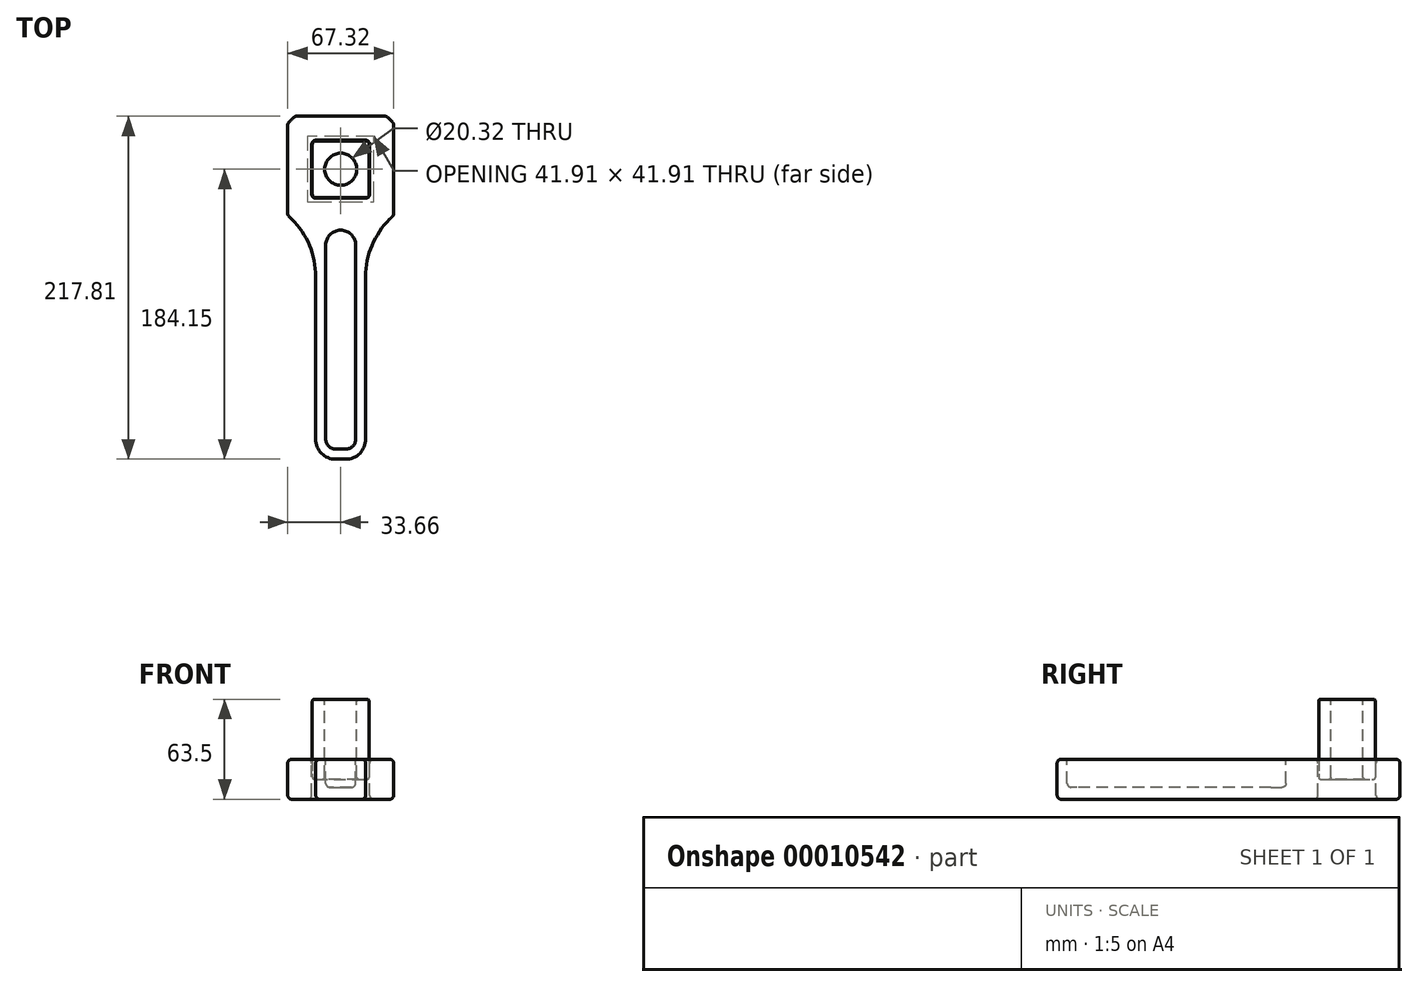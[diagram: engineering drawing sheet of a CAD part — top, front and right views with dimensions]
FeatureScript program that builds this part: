
annotation { "Feature Type Name" : "Feature", "Feature Type Description" : "" }
export const myFeature = defineFeature(function(context is Context, id is Id, definition is map)
    precondition{}
    {
        {
            var Q0;
            Q0=qCreatedBy(makeId("Top.planeOp"),FACE);
            var sketch = newSketch(context, id + "F0", { "sketchPlane" : qUnion([Q0])});
            skCircle(sketch, "E0", {"center": v(0, 0) * mm, "radius": 44.45 * mm});
            skLineSegment(sketch, "E1.bottom", {"start": v(-15.87, 0) * mm, "end": v(15.87, 0) * mm});
            skLineSegment(sketch, "E1.top", {"start": v(-15.87, -184.15) * mm, "end": v(15.88, -184.15) * mm});
            skLineSegment(sketch, "E1.left", {"start": v(-15.87, 0) * mm, "end": v(-15.87, -184.15) * mm});
            skLineSegment(sketch, "E1.right", {"start": v(15.88, 0) * mm, "end": v(15.88, -184.15) * mm});
            skLineSegment(sketch, "E2", {"start": v(0, 0) * mm, "end": v(0, -184.15) * mm, "construction": true});
            skSolve(sketch);
        }
        {
            var Q0;
            Q0 = qSketchRegion(id + "F0", true);
            extrude(context, id + "F1", {"entities" : qUnion([Q0]), "depth" : 25.4 * mm, "symmetric" : true});
        }
        {
            var Q0;
            Q0=makeQuery(id+"F1.opExtrude","CAP_FACE",FACE,{"disambiguationData":[OSD([sQuery(id+"F0.wireOp",EDGE,"E0"),sQuery(id+"F0.wireOp",EDGE,"E1.top"),sQuery(id+"F0.wireOp",EDGE,"E1.left"),sQuery(id+"F0.wireOp",EDGE,"E1.right")])],"isStart":false});
            var sketch = newSketch(context, id + "F2", { "sketchPlane" : qUnion([Q0])});
            skLineSegment(sketch, "E3.bottom", {"start": v(-18.42, 18.41) * mm, "end": v(18.41, 18.41) * mm});
            skLineSegment(sketch, "E3.top", {"start": v(-18.41, -18.41) * mm, "end": v(18.41, -18.41) * mm});
            skLineSegment(sketch, "E3.left", {"start": v(-18.41, 18.41) * mm, "end": v(-18.41, -18.41) * mm});
            skLineSegment(sketch, "E3.right", {"start": v(18.41, 18.41) * mm, "end": v(18.42, -18.41) * mm});
            skLineSegment(sketch, "E4", {"start": v(0, 0) * mm, "end": v(0, -18.41) * mm, "construction": true});
            skLineSegment(sketch, "E5", {"start": v(0, 0) * mm, "end": v(18.41, 0) * mm, "construction": true});
            skSolve(sketch);
        }
        {
            var Q0;
            Q0 = qSketchRegion(id + "F2", true);
            extrude(context, id + "F3", {"entities" : qUnion([Q0]), "operationType" : NewBodyOperationType.REMOVE, "endBound" : BoundingType.UP_TO_NEXT, "oppositeDirection" : true, "depth" : 25.4 * mm});
        }
        {
            var Q0;
            Q0=makeQuery(id+"F1.opExtrude","SWEPT_EDGE",EDGE,{"disambiguationData":[OSD([sQuery(id+"F0.wireOp",EDGE,"E0"),sQuery(id+"F0.wireOp",EDGE,"E1.right")])]});
            var Q1;
            Q1=makeQuery(id+"F1.opExtrude","SWEPT_EDGE",EDGE,{"disambiguationData":[OSD([sQuery(id+"F0.wireOp",EDGE,"E0"),sQuery(id+"F0.wireOp",EDGE,"E1.left")])]});
            fillet(context, id + "F4", {"entities" : qUnion([Q0, Q1]), "radius" : 50.8 * mm, "tangentPropagation" : true, "allowEdgeOverflow" : false});
        }
        {
            var Q0;
            Q0=makeQuery(id+"F1.opExtrude","SWEPT_EDGE",EDGE,{"disambiguationData":[OSD([sQuery(id+"F0.wireOp",EDGE,"E1.top"),sQuery(id+"F0.wireOp",EDGE,"E1.right")])]});
            var Q1;
            Q1=makeQuery(id+"F1.opExtrude","SWEPT_EDGE",EDGE,{"disambiguationData":[OSD([sQuery(id+"F0.wireOp",EDGE,"E1.top"),sQuery(id+"F0.wireOp",EDGE,"E1.left")])]});
            fillet(context, id + "F5", {"entities" : qUnion([Q0, Q1]), "radius" : 12.7 * mm, "tangentPropagation" : true, "allowEdgeOverflow" : false});
        }
        {
            var Q0;
            Q0=makeQuery(id+"F1.opExtrude","CAP_FACE",FACE,{"disambiguationData":[OSD([sQuery(id+"F0.wireOp",EDGE,"E0"),sQuery(id+"F0.wireOp",EDGE,"E1.top"),sQuery(id+"F0.wireOp",EDGE,"E1.left"),sQuery(id+"F0.wireOp",EDGE,"E1.right")])],"isStart":false});
            var sketch = newSketch(context, id + "F6", { "sketchPlane" : qUnion([Q0])});
            skLineSegment(sketch, "E6.1", {"start": v(9.53, -48.26) * mm, "end": v(9.53, -171.45) * mm});
            skArc(sketch, "E6.2", {"start": v(3.18, -177.8) * mm, "mid": v(7.67, -175.94) * mm, "end": v(9.53, -171.45) * mm});
            skLineSegment(sketch, "E6.4", {"start": v(-9.53, -48.26) * mm, "end": v(-9.53, -171.45) * mm});
            skArc(sketch, "E6.5", {"start": v(-9.53, -171.45) * mm, "mid": v(-7.67, -175.94) * mm, "end": v(-3.17, -177.8) * mm});
            skLineSegment(sketch, "E6.6", {"start": v(-3.17, -177.8) * mm, "end": v(3.18, -177.8) * mm});
            skArc(sketch, "E7", {"start": v(-9.53, -48.26) * mm, "mid": v(0, -38.74) * mm, "end": v(9.53, -48.26) * mm});
            skSolve(sketch);
        }
        {
            var Q0;
            Q0 = qSketchRegion(id + "F6", true);
            extrude(context, id + "F7", {"entities" : qUnion([Q0]), "operationType" : NewBodyOperationType.REMOVE, "oppositeDirection" : true, "depth" : 17.78 * mm});
        }
        {
            var Q0;
            Q0=makeQuery(id+"F1.opExtrude","CAP_FACE",FACE,{"disambiguationData":[OSD([sQuery(id+"F0.wireOp",EDGE,"E0"),sQuery(id+"F0.wireOp",EDGE,"E1.top"),sQuery(id+"F0.wireOp",EDGE,"E1.left"),sQuery(id+"F0.wireOp",EDGE,"E1.right")])],"isStart":false});
            var sketch = newSketch(context, id + "F8", { "sketchPlane" : qUnion([Q0])});
            skLineSegment(sketch, "E8.0", {"start": v(33.65, 33.66) * mm, "end": v(33.66, -29.04) * mm});
            skLineSegment(sketch, "E8.1", {"start": v(-33.66, 33.66) * mm, "end": v(33.65, 33.66) * mm});
            skLineSegment(sketch, "E8.2", {"start": v(-33.66, 33.66) * mm, "end": v(-33.66, -29.04) * mm});
            skSolve(sketch);
        }
        {
            var Q0;
            {var subQ0=sQuery(id+"F8.wireOp",EDGE,"E8.2");var subQ1=makeQuery(id+"F1.opExtrude","CAP_EDGE",EDGE,{"disambiguationData":[OSD([sQuery(id+"F0.wireOp",EDGE,"E0")])],"isStart":false});var subQ2=makeQuery(id+"F8.imprint","INTERSECT",VERTEX,{"disambiguationData":[OD(0.0)],"derivedFrom":[subQ1,subQ0]});Q0=makeQuery(id+"F8.imprint","IMPRINT",FACE,{"disambiguationData":[TD([[makeQuery(id+"F8.imprint","IMPRINT",EDGE,{"disambiguationData":[TD([[subQ2,1.0]])],"derivedFrom":subQ0}),-1.0]])]});}
            var Q1;
            {var subQ0=sQuery(id+"F8.wireOp",EDGE,"E8.1");var subQ1=makeQuery(id+"F1.opExtrude","CAP_EDGE",EDGE,{"disambiguationData":[OSD([sQuery(id+"F0.wireOp",EDGE,"E0")])],"isStart":false});var subQ2=makeQuery(id+"F8.imprint","INTERSECT",VERTEX,{"disambiguationData":[OD(0.0)],"derivedFrom":[subQ1,subQ0]});Q1=makeQuery(id+"F8.imprint","IMPRINT",FACE,{"disambiguationData":[TD([[makeQuery(id+"F8.imprint","IMPRINT",EDGE,{"disambiguationData":[TD([[subQ2,-1.0]])],"derivedFrom":subQ0}),1.0]])]});}
            var Q2;
            {var subQ0=sQuery(id+"F8.wireOp",EDGE,"E8.0");var subQ1=makeQuery(id+"F1.opExtrude","CAP_EDGE",EDGE,{"disambiguationData":[OSD([sQuery(id+"F0.wireOp",EDGE,"E0")])],"isStart":false});var subQ2=makeQuery(id+"F8.imprint","INTERSECT",VERTEX,{"disambiguationData":[OD(0.0)],"derivedFrom":[subQ1,subQ0]});Q2=makeQuery(id+"F8.imprint","IMPRINT",FACE,{"disambiguationData":[TD([[makeQuery(id+"F8.imprint","IMPRINT",EDGE,{"disambiguationData":[TD([[subQ2,1.0]])],"derivedFrom":subQ0}),1.0]])]});}
            extrude(context, id + "F9", {"entities" : qUnion([Q0, Q1, Q2]), "operationType" : NewBodyOperationType.REMOVE, "endBound" : BoundingType.UP_TO_NEXT, "oppositeDirection" : true, "depth" : 25.4 * mm});
        }
        {
            var Q0;
            Q0=makeQuery(id+"F3.boolean.opBoolean","COPY",FACE,{"derivedFrom":makeQuery(id+"F3.opExtrude","SWEPT_FACE",FACE,{"disambiguationData":[OSD([sQuery(id+"F2.wireOp",EDGE,"E3.bottom")])]})});
            var Q1;
            Q1=makeQuery(id+"F3.boolean.opBoolean","COPY",FACE,{"derivedFrom":makeQuery(id+"F3.opExtrude","SWEPT_FACE",FACE,{"disambiguationData":[OSD([sQuery(id+"F2.wireOp",EDGE,"E3.right")])]})});
            var Q2;
            Q2=makeQuery(id+"F3.boolean.opBoolean","COPY",FACE,{"derivedFrom":makeQuery(id+"F3.opExtrude","SWEPT_FACE",FACE,{"disambiguationData":[OSD([sQuery(id+"F2.wireOp",EDGE,"E3.left")])]})});
            var Q3;
            Q3=makeQuery(id+"F3.boolean.opBoolean","COPY",FACE,{"derivedFrom":makeQuery(id+"F3.opExtrude","SWEPT_FACE",FACE,{"disambiguationData":[OSD([sQuery(id+"F2.wireOp",EDGE,"E3.top")])]})});
            fillet(context, id + "F10", {"entities" : qUnion([Q0, Q1, Q2, Q3]), "radius" : 2.54 * mm, "tangentPropagation" : true, "allowEdgeOverflow" : false});
        }
        {
            var Q0;
            Q0=makeQuery(id+"F1.opExtrude","CAP_EDGE",EDGE,{"disambiguationData":[OSD([sQuery(id+"F0.wireOp",EDGE,"E1.left")])],"isStart":false});
            var Q1;
            Q1=makeQuery(id+"F7.boolean.opBoolean","COPY",FACE,{"derivedFrom":makeQuery(id+"F7.opExtrude","CAP_FACE",FACE,{"disambiguationData":[OSD([sQuery(id+"F6.wireOp",EDGE,"E6.1"),sQuery(id+"F6.wireOp",EDGE,"E6.2"),sQuery(id+"F6.wireOp",EDGE,"E6.4"),sQuery(id+"F6.wireOp",EDGE,"E6.5"),sQuery(id+"F6.wireOp",EDGE,"E6.6"),sQuery(id+"F6.wireOp",EDGE,"E7")])],"isStart":false})});
            var Q2;
            Q2=makeQuery(id+"F7.boolean.opBoolean","COPY",EDGE,{"derivedFrom":makeQuery(id+"F7.opExtrude","CAP_EDGE",EDGE,{"disambiguationData":[OSD([sQuery(id+"F6.wireOp",EDGE,"E7")])],"isStart":true})});
            var Q3;
            Q3=makeQuery(id+"F1.opExtrude","CAP_EDGE",EDGE,{"disambiguationData":[OSD([sQuery(id+"F0.wireOp",EDGE,"E1.left")])],"isStart":true});
            var Q4;
            Q4=makeQuery(id+"F9.boolean.opBoolean","COPY",FACE,{"derivedFrom":makeQuery(id+"F9.opExtrude","SWEPT_FACE",FACE,{"disambiguationData":[OSD([sQuery(id+"F8.wireOp",EDGE,"E8.2")])]})});
            var Q5;
            {var subQ0=sQuery(id+"F0.wireOp",EDGE,"E1.right");var subQ1=sQuery(id+"F0.wireOp",EDGE,"E1.left");var subQ2=sQuery(id+"F0.wireOp",EDGE,"E1.top");var subQ3=sQuery(id+"F0.wireOp",EDGE,"E0");Q5=makeQuery(id+"F9.boolean.opBoolean","SPLIT",FACE,{"disambiguationData":[TD([makeQuery(id+"F1.opExtrude","CAP_FACE",FACE,{"disambiguationData":[OSD([subQ3,subQ2,subQ1,subQ0])],"isStart":true}),makeQuery(id+"F1.opExtrude","CAP_FACE",FACE,{"disambiguationData":[OSD([subQ3,subQ2,subQ1,subQ0])],"isStart":false}),makeQuery(id+"F9.opExtrude","SWEPT_FACE",FACE,{"disambiguationData":[OSD([sQuery(id+"F8.wireOp",EDGE,"E8.1")])]}),makeQuery(id+"F9.opExtrude","SWEPT_FACE",FACE,{"disambiguationData":[OSD([sQuery(id+"F8.wireOp",EDGE,"E8.2")])]})])],"derivedFrom":makeQuery(id+"F1.opExtrude","SWEPT_FACE",FACE,{"disambiguationData":[OSD([subQ3])]})});}
            var Q6;
            Q6=makeQuery(id+"F9.boolean.opBoolean","COPY",FACE,{"derivedFrom":makeQuery(id+"F9.opExtrude","SWEPT_FACE",FACE,{"disambiguationData":[OSD([sQuery(id+"F8.wireOp",EDGE,"E8.1")])]})});
            var Q7;
            {var subQ0=sQuery(id+"F0.wireOp",EDGE,"E1.right");var subQ1=sQuery(id+"F0.wireOp",EDGE,"E1.left");var subQ2=sQuery(id+"F0.wireOp",EDGE,"E1.top");var subQ3=sQuery(id+"F0.wireOp",EDGE,"E0");Q7=makeQuery(id+"F9.boolean.opBoolean","SPLIT",FACE,{"disambiguationData":[TD([makeQuery(id+"F1.opExtrude","CAP_FACE",FACE,{"disambiguationData":[OSD([subQ3,subQ2,subQ1,subQ0])],"isStart":true}),makeQuery(id+"F1.opExtrude","CAP_FACE",FACE,{"disambiguationData":[OSD([subQ3,subQ2,subQ1,subQ0])],"isStart":false}),makeQuery(id+"F9.opExtrude","SWEPT_FACE",FACE,{"disambiguationData":[OSD([sQuery(id+"F8.wireOp",EDGE,"E8.0")])]}),makeQuery(id+"F9.opExtrude","SWEPT_FACE",FACE,{"disambiguationData":[OSD([sQuery(id+"F8.wireOp",EDGE,"E8.1")])]})])],"derivedFrom":makeQuery(id+"F1.opExtrude","SWEPT_FACE",FACE,{"disambiguationData":[OSD([subQ3])]})});}
            var Q8;
            Q8=makeQuery(id+"F9.boolean.opBoolean","COPY",FACE,{"derivedFrom":makeQuery(id+"F9.opExtrude","SWEPT_FACE",FACE,{"disambiguationData":[OSD([sQuery(id+"F8.wireOp",EDGE,"E8.0")])]})});
            fillet(context, id + "F11", {"entities" : qUnion([Q0, Q1, Q2, Q3, Q4, Q5, Q6, Q7, Q8]), "radius" : 2.54 * mm, "tangentPropagation" : true, "allowEdgeOverflow" : false});
        }
        {
            var Q0;
            Q0=qCreatedBy(makeId("Top.planeOp"),FACE);
            var sketch = newSketch(context, id + "F12", { "sketchPlane" : qUnion([Q0])});
            skArc(sketch, "E9.0", {"start": v(18.03, 15.88) * mm, "mid": v(17.4, 17.4) * mm, "end": v(15.87, 18.03) * mm});
            skLineSegment(sketch, "E9.1", {"start": v(18.03, -15.88) * mm, "end": v(18.03, 15.88) * mm});
            skLineSegment(sketch, "E9.2", {"start": v(15.87, 18.03) * mm, "end": v(-15.88, 18.03) * mm});
            skArc(sketch, "E9.3", {"start": v(15.88, -18.03) * mm, "mid": v(17.4, -17.4) * mm, "end": v(18.03, -15.88) * mm});
            skArc(sketch, "E9.4", {"start": v(-15.88, 18.03) * mm, "mid": v(-17.4, 17.4) * mm, "end": v(-18.03, 15.88) * mm});
            skLineSegment(sketch, "E9.5", {"start": v(-18.03, 15.88) * mm, "end": v(-18.03, -15.88) * mm});
            skArc(sketch, "E9.6", {"start": v(-18.03, -15.88) * mm, "mid": v(-17.4, -17.4) * mm, "end": v(-15.88, -18.03) * mm});
            skLineSegment(sketch, "E9.7", {"start": v(-15.87, -18.03) * mm, "end": v(15.88, -18.03) * mm});
            skSolve(sketch);
        }
        {
            var Q0;
            Q0 = qSketchRegion(id + "F12", true);
            extrude(context, id + "F13", {"entities" : qUnion([Q0]), "depth" : 50.8 * mm});
        }
        {
            var Q0;
            Q0=makeQuery(id+"F13.opExtrude","CAP_FACE",FACE,{"disambiguationData":[OSD([sQuery(id+"F12.wireOp",EDGE,"E9.0"),sQuery(id+"F12.wireOp",EDGE,"E9.1"),sQuery(id+"F12.wireOp",EDGE,"E9.2"),sQuery(id+"F12.wireOp",EDGE,"E9.3"),sQuery(id+"F12.wireOp",EDGE,"E9.4"),sQuery(id+"F12.wireOp",EDGE,"E9.5"),sQuery(id+"F12.wireOp",EDGE,"E9.6"),sQuery(id+"F12.wireOp",EDGE,"E9.7")])],"isStart":false});
            var sketch = newSketch(context, id + "F14", { "sketchPlane" : qUnion([Q0])});
            skCircle(sketch, "E10", {"center": v(0, 0) * mm, "radius": 10.16 * mm});
            skSolve(sketch);
        }
        {
            var Q0;
            Q0 = qSketchRegion(id + "F14", true);
            extrude(context, id + "F15", {"entities" : qUnion([Q0]), "operationType" : NewBodyOperationType.REMOVE, "endBound" : BoundingType.UP_TO_NEXT, "oppositeDirection" : true, "depth" : 25.4 * mm});
        }
        {
            var Q0;
            Q0=makeQuery(id+"F13.opExtrude","CAP_FACE",FACE,{"disambiguationData":[OSD([sQuery(id+"F12.wireOp",EDGE,"E9.0"),sQuery(id+"F12.wireOp",EDGE,"E9.1"),sQuery(id+"F12.wireOp",EDGE,"E9.2"),sQuery(id+"F12.wireOp",EDGE,"E9.3"),sQuery(id+"F12.wireOp",EDGE,"E9.4"),sQuery(id+"F12.wireOp",EDGE,"E9.5"),sQuery(id+"F12.wireOp",EDGE,"E9.6"),sQuery(id+"F12.wireOp",EDGE,"E9.7")])],"isStart":false});
            var Q1;
            Q1=makeQuery(id+"F13.opExtrude","CAP_FACE",FACE,{"disambiguationData":[OSD([sQuery(id+"F12.wireOp",EDGE,"E9.0"),sQuery(id+"F12.wireOp",EDGE,"E9.1"),sQuery(id+"F12.wireOp",EDGE,"E9.2"),sQuery(id+"F12.wireOp",EDGE,"E9.3"),sQuery(id+"F12.wireOp",EDGE,"E9.4"),sQuery(id+"F12.wireOp",EDGE,"E9.5"),sQuery(id+"F12.wireOp",EDGE,"E9.6"),sQuery(id+"F12.wireOp",EDGE,"E9.7")])],"isStart":true});
            fillet(context, id + "F16", {"entities" : qUnion([Q0, Q1]), "radius" : 1.27 * mm, "tangentPropagation" : true, "allowEdgeOverflow" : false});
        }
    });
